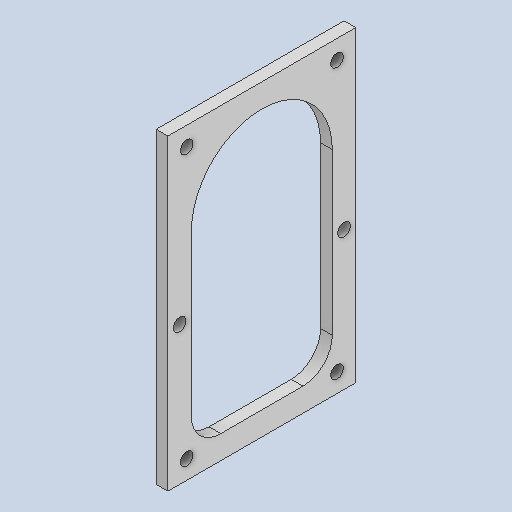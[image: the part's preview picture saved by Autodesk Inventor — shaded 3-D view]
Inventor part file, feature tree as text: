
AUTODESK INVENTOR PART (.ipt)
format: ipt  version: 2023 (Build 270158000, 158)  size: 280,064 bytes
history: native  units: in
note: dims shown in document units (in); Inventor stores cm internally (conversion verified against a paired STEP export)
features: extrude x1
ambient origin geometry x8: Origin, YZ Plane, XZ Plane, XY Plane, X Axis, Y Axis, Z Axis, Center Point
bodies: Solid1 (feature_tree)
feature tree (1):
  extrude  "Extrusion1"  Depth=3.275in
